FCSTD DOCUMENT  (FreeCAD 0.22R36117 (Git))
Label: molding calculations
License: All rights reserved
LicenseURL: http://en.wikipedia.org/wiki/All_rights_reserved
objects: Sketcher::SketchObject×1, PartDesign::Body×1
note: 2 computed .brp shape members not serialized (recipe doc carries the construction recipe); baked Part::Feature solids carry a one-line shape summary decoded from their .brp

FEATURE [Sketcher::SketchObject] Sketch
  FullyConstrained = false
  MapMode = 5
  Support = -> [XY_Plane]
  sketch-geometry (24):
    g0: LineSegment StartX=-71.4785 StartY=8.99977 StartZ=0 EndX=-71.4785 EndY=-39.9207 EndZ=0
    g1: LineSegment StartX=-71.4785 StartY=-39.9207 StartZ=0 EndX=66.0128 EndY=-39.9207 EndZ=0
    g2: LineSegment StartX=66.0128 StartY=-39.9207 StartZ=0 EndX=66.0128 EndY=8.99977 EndZ=0
    g3: LineSegment StartX=66.0128 StartY=8.99977 StartZ=0 EndX=-71.4785 EndY=8.99977 EndZ=0
    g4: LineSegment StartX=-71.748 StartY=74.3969 StartZ=0 EndX=-71.748 EndY=59.7998 EndZ=0
    g5: LineSegment StartX=-71.748 StartY=59.7998 StartZ=0 EndX=159.953 EndY=59.7998 EndZ=0
    g6: LineSegment StartX=159.953 StartY=59.7998 StartZ=0 EndX=159.953 EndY=74.3969 EndZ=0
    g7: LineSegment StartX=159.953 StartY=74.3969 StartZ=0 EndX=-71.748 EndY=74.3969 EndZ=0
    g8: LineSegment StartX=69.1878 StartY=2.64977 StartZ=0 EndX=69.1878 EndY=-80.4521 EndZ=0
    g9: LineSegment StartX=69.1878 StartY=-80.4521 StartZ=0 EndX=88.2378 EndY=-80.4521 EndZ=0
    g10: LineSegment StartX=88.2378 StartY=-80.4521 StartZ=0 EndX=88.2378 EndY=2.64977 EndZ=0
    g11: LineSegment StartX=88.2378 StartY=2.64977 StartZ=0 EndX=69.1878 EndY=2.64977 EndZ=0
    g12: LineSegment StartX=85.0628 StartY=26.9603 StartZ=0 EndX=127.095 EndY=59.7998 EndZ=0
    g13: LineSegment StartX=85.0628 StartY=26.9603 StartZ=0 EndX=85.0628 EndY=8.99977 EndZ=0
    g14: LineSegment StartX=85.0628 StartY=8.99977 StartZ=0 EndX=91.4128 EndY=8.99977 EndZ=0
    g15: LineSegment StartX=145.056 StartY=53.4498 StartZ=0 EndX=145.056 EndY=59.7998 EndZ=0
    g16: LineSegment StartX=145.056 StartY=59.7998 StartZ=0 EndX=127.095 EndY=59.7998 EndZ=0
    g17: LineSegment StartX=85.0628 StartY=26.9603 StartZ=0 EndX=80.2924 EndY=23.2332 EndZ=0
    g18: LineSegment StartX=80.2924 StartY=23.2332 StartZ=0 EndX=91.4128 EndY=8.99977 EndZ=0
    g19: LineSegment StartX=85.0628 StartY=8.99977 StartZ=0 EndX=145.056 EndY=59.7998 EndZ=0
    g20: ArcOfCircle CenterX=143.971 CenterY=0.164731 CenterZ=0 NormalX=0 NormalY=0 NormalZ=1 AngleXU=0 Radius=53.2961 StartAngle=1.55045 EndAngle=2.97505
    g21: LineSegment StartX=46.9628 StartY=8.99977 StartZ=0 EndX=85.0628 EndY=8.99977 EndZ=0
    g22: LineSegment StartX=85.0628 StartY=8.99977 StartZ=0 EndX=85.0628 EndY=28.0498 EndZ=0
    g23: LineSegment StartX=85.0628 StartY=28.0498 StartZ=0 EndX=46.9628 EndY=28.0498 EndZ=0
  constraints (63):
    c: Coincident(g0,g1)
    c: Coincident(g1,g2)
    c: Coincident(g3,g0)
    c: Vertical(g0)
    c: Vertical(g2)
    c: Horizontal(g1)
    c: Horizontal(g3)
    c: Coincident(g4,g5)
    c: Coincident(g5,g6)
    c: Coincident(g6,g7)
    c: Coincident(g7,g4)
    c: Vertical(g4)
    c: Vertical(g6)
    c: Horizontal(g5)
    c: Horizontal(g7)
    c: DistanceY(g2,g5) = 50.8
    c: Coincident(g8,g9)
    c: Coincident(g9,g10)
    c: Coincident(g10,g11)
    c: Coincident(g11,g8)
    c: Vertical(g8)
    c: Vertical(g10)
    c: Horizontal(g9)
    c: Horizontal(g11)
    c: DistanceX(g11,g11) = 19.05
    c: DistanceY(g8,g2) = 6.35
    c: DistanceX(g2,g8) = 3.175
    c: Coincident(g13,g12)
    c: Vertical(g13)
    c: Coincident(g13,g14)
    c: Horizontal(g14)
    c: Vertical(g15)
    c: Coincident(g15,g16)
    c: Horizontal(g16)
    c: Coincident(g12,g16)
    c: Equal(g16,g13)
    c: Equal(g14,g15)
    c: Angle(g14,g12) = 0.663225
    c: Distance(g14,g12) = 19.05
    c: DistanceX(g14,g14) = 6.35
    c: Coincident(g17,g12)
    c: Parallel(g17,g12)
    c: Coincident(g18,g17)
    c: Perpendicular(g17,g18)
    c: Coincident(g18,g14)
    c: Coincident(g19,g13)
    c: Coincident(g19,g15)
    c: Distance(g19) = 78.6118
    c: PointOnObject(g15,g5)
    c: Coincident(g20,g14)
    c: Coincident(g20,g15)
    c: Horizontal(g21)
    c: Coincident(g22,g21)
    c: Vertical(g22)
    c: DistanceY(g22,g22) = 19.05
    c: DistanceX(g21,g3) = 19.05
    c: Coincident(g3,g2)
    c: DistanceX(g21,g21) = 38.1
    c: PointOnObject(g21,g3)
    c: Coincident(g13,g21)
    c: Coincident(g23,g22)
    c: Horizontal(g23)
    c: Vertical(g23,g21)
FEATURE [PartDesign::Body] Body
  Group = -> [Sketch]
  Origin = -> Origin
